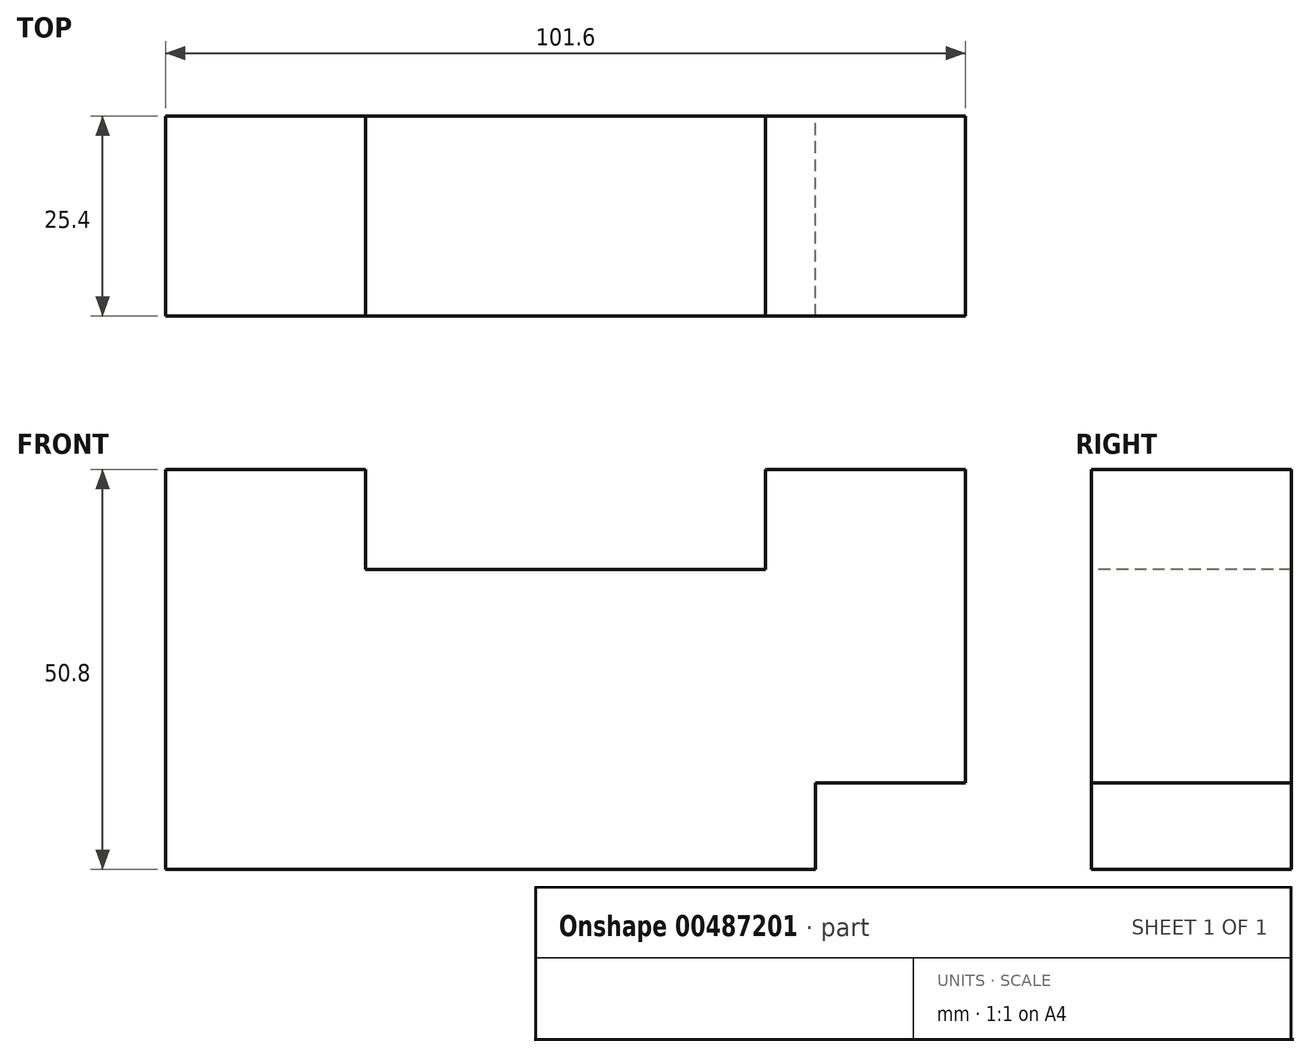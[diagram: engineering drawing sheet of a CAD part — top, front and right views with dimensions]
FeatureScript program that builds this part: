
annotation { "Feature Type Name" : "Feature", "Feature Type Description" : "" }
export const myFeature = defineFeature(function(context is Context, id is Id, definition is map)
    precondition{}
    {
        {
            var Q0;
            Q0=qCreatedBy(makeId("Front.planeOp"),FACE);
            var sketch = newSketch(context, id + "F0", { "sketchPlane" : qUnion([Q0])});
            skLineSegment(sketch, "E0.bottom", {"start": v(50.8, 25.4) * mm, "end": v(-50.8, 25.4) * mm});
            skLineSegment(sketch, "E0.top", {"start": v(50.8, -25.4) * mm, "end": v(-50.8, -25.4) * mm});
            skLineSegment(sketch, "E0.left", {"start": v(50.8, 25.4) * mm, "end": v(50.8, -25.4) * mm});
            skLineSegment(sketch, "E0.right", {"start": v(-50.8, 25.4) * mm, "end": v(-50.8, -25.4) * mm});
            skPoint(sketch, "E0.middle", {"position": v(0, 0) * mm});
            skSolve(sketch);
        }
        {
            var Q0;
            Q0 = qSketchRegion(id + "F0", true);
            extrude(context, id + "F1", {"entities" : qUnion([Q0]), "depth" : 25.4 * mm});
        }
        {
            var Q0;
            Q0=makeQuery(id+"F1.opExtrude","SWEPT_FACE",FACE,{"disambiguationData":[OSD([sQuery(id+"F0.wireOp",EDGE,"E0.bottom")])]});
            var sketch = newSketch(context, id + "F2", { "sketchPlane" : qUnion([Q0])});
            skLineSegment(sketch, "E1.bottom", {"start": v(-25.4, 0) * mm, "end": v(25.4, 0) * mm});
            skLineSegment(sketch, "E1.top", {"start": v(-25.4, -25.4) * mm, "end": v(25.4, -25.4) * mm});
            skLineSegment(sketch, "E1.left", {"start": v(-25.4, 0) * mm, "end": v(-25.4, -25.4) * mm});
            skLineSegment(sketch, "E1.right", {"start": v(25.4, 0) * mm, "end": v(25.4, -25.4) * mm});
            skSolve(sketch);
        }
        {
            var Q0;
            Q0 = qSketchRegion(id + "F2", true);
            extrude(context, id + "F3", {"entities" : qUnion([Q0]), "operationType" : NewBodyOperationType.REMOVE, "oppositeDirection" : true, "depth" : 12.7 * mm});
        }
        {
            var Q0;
            Q0=makeQuery(id+"F1.opExtrude","SWEPT_FACE",FACE,{"disambiguationData":[OSD([sQuery(id+"F0.wireOp",EDGE,"E0.left")])]});
            var sketch = newSketch(context, id + "F4", { "sketchPlane" : qUnion([Q0])});
            skLineSegment(sketch, "E2.bottom", {"start": v(-25.4, -14.39) * mm, "end": v(0, -14.39) * mm});
            skLineSegment(sketch, "E2.top", {"start": v(-25.4, -25.4) * mm, "end": v(0, -25.4) * mm});
            skLineSegment(sketch, "E2.left", {"start": v(-25.4, -14.39) * mm, "end": v(-25.4, -25.4) * mm});
            skLineSegment(sketch, "E2.right", {"start": v(0, -14.39) * mm, "end": v(0, -25.4) * mm});
            skSolve(sketch);
        }
        {
            var Q0;
            Q0=makeQuery(id+"F4.imprint","IMPRINT",FACE,{"disambiguationData":[TD([[makeQuery(id+"F4.imprint","IMPRINT",EDGE,{"derivedFrom":sQuery(id+"F4.wireOp",EDGE,"E2.bottom")}),-1.0]])]});
            extrude(context, id + "F5", {"entities" : qUnion([Q0]), "operationType" : NewBodyOperationType.REMOVE, "oppositeDirection" : true, "depth" : 19.05 * mm});
        }
    });
